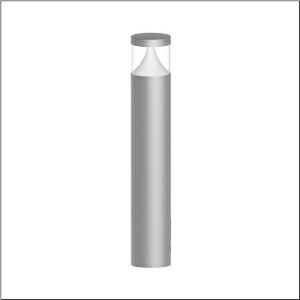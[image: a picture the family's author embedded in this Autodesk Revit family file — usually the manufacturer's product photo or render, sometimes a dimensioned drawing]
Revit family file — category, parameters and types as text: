
# Revit family: cl_31_poller_90_5cl444603
name_source: partatom
category: Lighting Fixtures
units: mm (PartAtom-declared; Revit-internal decimal feet)

## family parameters
Cut with Voids When Loaded = No
Host = Face
Light Source = No
Part Type = Normal
Room Calculation Point = No
Round Connector Dimension = Use Diameter
Shared = No

## types (1)
- --- (1 x LED, 1500 lm, 14 W, 3000K)
    Apparent Load = 14 VA
    CIE Flux Codes = 19 66 88 92 100
    Color Rendering = 80
    Color Temperature = 3000K
    Default Elevation = 1800 mm
    Description = CL 31 Bollard 90, bollard luminaire, primary light control with lens, of PC, primary optical cover: cover panel, of PC, transparent, secondary light control with reflector, of PC, primary light characteristic: asymmetric, LED, rated luminous flux: 1.500lm, luminous efficacy: 107lm/W, light colour: 830, colour temperature: 3000K, control gear: ECG DALI, with terminal, 5-pole, max. 2.5mm², mains connection: 220..240V, AC, 50/60Hz, rated input power: 14W, luminaire housing, of aluminium, powder-coated, Siteco® metallic grey, diameter: 170mm, height: 900mm, protection rating (complete): IP65, insulation class (complete): insulation class I (protective earthing), certification: CE, ENEC, impact resistance: IK10, permissible operating ambient temperature for outdoor applications: -20..+50°C, packaging unit: 1 piece
    Height = 200 mm  [stored 0.656168 ft]
    Lamp = 1 x LED
    Lamp Light Flux = 1500 lm
    Lamp Power = 14 W
    Lamp count = 1
    Length = 170 mm  [stored 0.557743 ft]
    Luminous efficacy = 107 lm/W
    Manufacturer = Siteco
    ModVariant = No
    Model = 5CL444603
    Mounting Place = Floor
    Mounting Type = Freestanding
    Number of Poles = 1
    OnlyDefault = Yes
    Power Factor = 1
    Product Name = CL 31 Poller 90
    Product group = bollard luminaire
    ProductGroupID = 1304
    Protection Class = Protection class I
    Protection Degree = IP 65
    RLX_Detail_Level = 1
    RLX_Emergency_Light_Flux = 0 lm
    RLX_Emergency_Type = 0
    RLX_Emergency_Type_DB = No
    RlxData = <blob elided: 64869 chars, md5=3199f4c5>
    Socket = socket
    Standby Power = 0 W
    System Light Flux = 1500 lm
    System Power = 14 W
    Type Comments = factory setting: luminous flux: 100 % | dim-lin: 254 | 350 mA
    Type Image = l_1006899.jpg
    URL = http://relux.com
    VarID = @adj_148335
    Voltage = 0 V
    Weight = 0.00 kg
    Width = 0 mm  [stored 0 ft]

note: [stored X ft] marks values corroborated as IEEE doubles in the binary element streams (Revit-internal decimal feet)

## geometry (parser evidence)
native form markers: Blend x4, Sweep x11
no freeform markers — native parametric forms only
